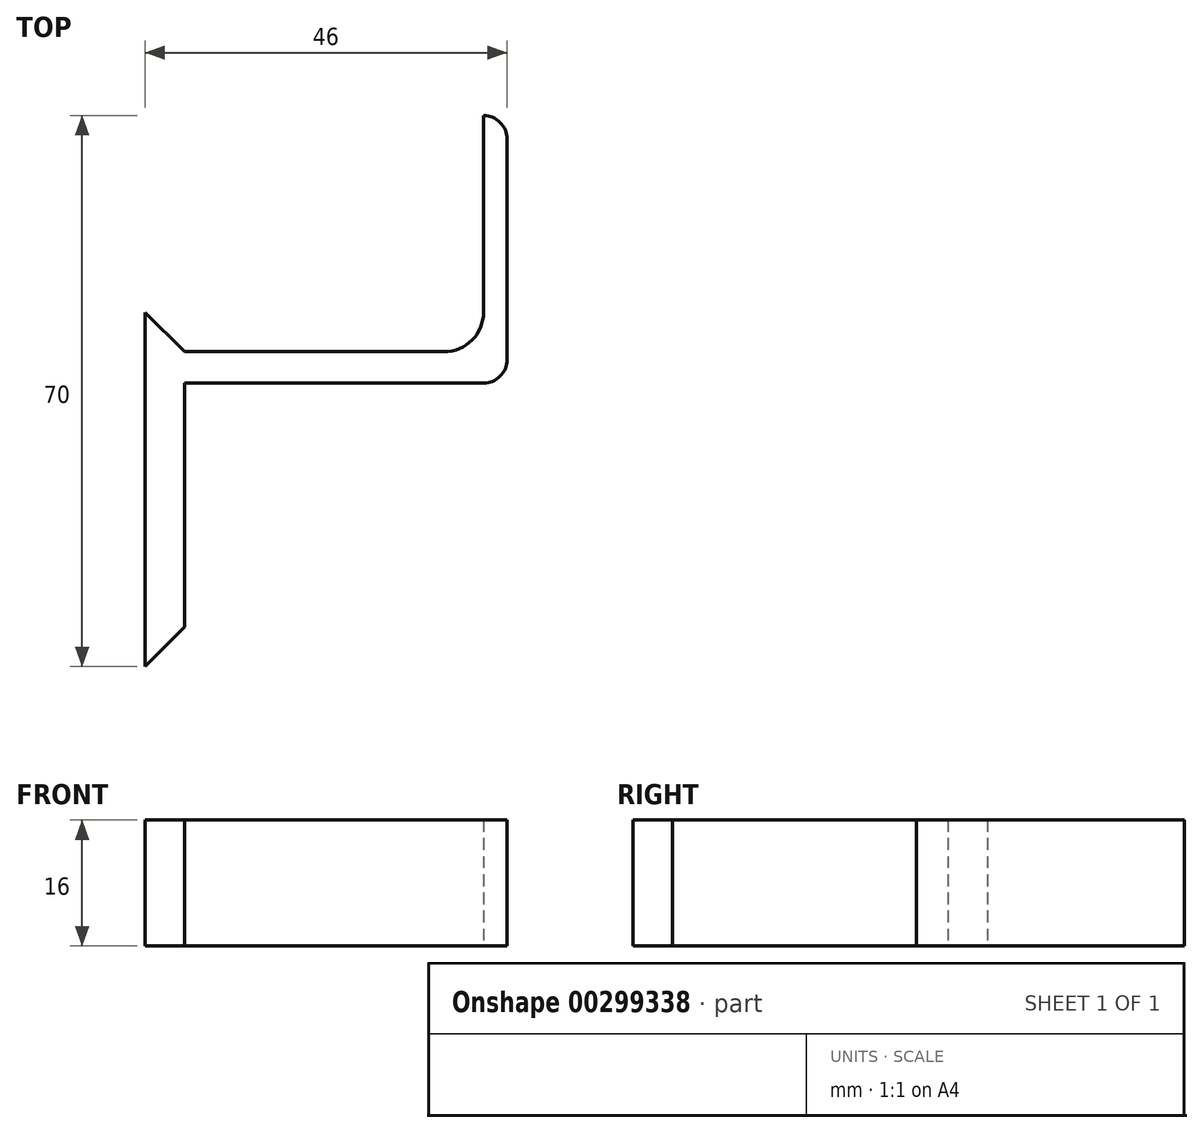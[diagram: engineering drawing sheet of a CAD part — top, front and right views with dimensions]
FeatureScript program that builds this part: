
annotation { "Feature Type Name" : "Feature", "Feature Type Description" : "" }
export const myFeature = defineFeature(function(context is Context, id is Id, definition is map)
    precondition{}
    {
        {
            var Q0;
            Q0=qCreatedBy(makeId("Top.planeOp"),FACE);
            var sketch = newSketch(context, id + "F0", { "sketchPlane" : qUnion([Q0])});
            skLineSegment(sketch, "E0", {"start": v(-35.28, 0) * mm, "end": v(-35.28, -40) * mm});
            skLineSegment(sketch, "E1", {"start": v(-35.28, 0) * mm, "end": v(2.72, 0) * mm});
            skLineSegment(sketch, "E2", {"start": v(2.72, 0) * mm, "end": v(2.72, 30) * mm});
            skLineSegment(sketch, "E3", {"start": v(2.72, 30) * mm, "end": v(5.72, 30) * mm});
            skLineSegment(sketch, "E4", {"start": v(5.72, 30) * mm, "end": v(5.72, 0) * mm});
            skLineSegment(sketch, "E5", {"start": v(5.72, 0) * mm, "end": v(2.72, 0) * mm});
            skLineSegment(sketch, "E6", {"start": v(5.72, 0) * mm, "end": v(5.72, -4) * mm});
            skLineSegment(sketch, "E7", {"start": v(5.72, -4) * mm, "end": v(-35.28, -4) * mm});
            skLineSegment(sketch, "E8", {"start": v(-35.28, 0) * mm, "end": v(-40.28, 0) * mm});
            skLineSegment(sketch, "E9", {"start": v(-40.28, 0) * mm, "end": v(-40.28, -40) * mm});
            skLineSegment(sketch, "E10", {"start": v(-40.28, -40) * mm, "end": v(-35.28, -40) * mm});
            skLineSegment(sketch, "E11", {"start": v(-40.28, 0) * mm, "end": v(-40.28, 5) * mm});
            skLineSegment(sketch, "E12", {"start": v(-40.28, 5) * mm, "end": v(-35.28, 5) * mm});
            skLineSegment(sketch, "E13", {"start": v(-35.28, 5) * mm, "end": v(-35.28, 0) * mm});
            skSolve(sketch);
        }
        {
            var Q0;
            Q0=makeQuery(id+"F0.imprint","IMPRINT",FACE,{"disambiguationData":[TD([[makeQuery(id+"F0.imprint","IMPRINT",EDGE,{"derivedFrom":sQuery(id+"F0.wireOp",EDGE,"E8")}),-1.0]])]});
            var Q1;
            {var subQ0=sQuery(id+"F0.wireOp",EDGE,"E8");Q1=makeQuery(id+"F0.imprint","IMPRINT",FACE,{"disambiguationData":[TD([[makeQuery(id+"F0.imprint","IMPRINT",EDGE,{"derivedFrom":subQ0}),1.0]])]});}
            var Q2;
            {var subQ0=sQuery(id+"F0.wireOp",EDGE,"E1");Q2=makeQuery(id+"F0.imprint","IMPRINT",FACE,{"disambiguationData":[TD([[makeQuery(id+"F0.imprint","IMPRINT",EDGE,{"derivedFrom":subQ0}),-1.0]])]});}
            var Q3;
            Q3=makeQuery(id+"F0.imprint","IMPRINT",FACE,{"disambiguationData":[TD([[makeQuery(id+"F0.imprint","IMPRINT",EDGE,{"derivedFrom":sQuery(id+"F0.wireOp",EDGE,"E2")}),-1.0]])]});
            extrude(context, id + "F1", {"entities" : qUnion([Q0, Q1, Q2, Q3]), "depth" : 16 * mm});
        }
        {
            var Q0;
            Q0=makeQuery(id+"F1.opExtrude","SWEPT_EDGE",EDGE,{"disambiguationData":[OSD([sQuery(id+"F0.wireOp",EDGE,"E12"),sQuery(id+"F0.wireOp",EDGE,"E13")])]});
            chamfer(context, id + "F2", {"entities" : qUnion([Q0]), "width" : 5 * mm, "tangentPropagation" : true});
        }
        {
            var Q0;
            Q0=makeQuery(id+"F1.opExtrude","SWEPT_EDGE",EDGE,{"disambiguationData":[OSD([sQuery(id+"F0.wireOp",EDGE,"E0"),sQuery(id+"F0.wireOp",EDGE,"E10")])]});
            chamfer(context, id + "F3", {"entities" : qUnion([Q0]), "width" : 5 * mm, "tangentPropagation" : true});
        }
        {
            var Q0;
            Q0=makeQuery(id+"F1.opExtrude","SWEPT_EDGE",EDGE,{"disambiguationData":[OSD([sQuery(id+"F0.wireOp",EDGE,"E1"),sQuery(id+"F0.wireOp",EDGE,"E2"),sQuery(id+"F0.wireOp",EDGE,"E5")])]});
            fillet(context, id + "F4", {"entities" : qUnion([Q0]), "radius" : 5 * mm, "tangentPropagation" : true, "allowEdgeOverflow" : false});
        }
        {
            var Q0;
            Q0=makeQuery(id+"F1.opExtrude","SWEPT_EDGE",EDGE,{"disambiguationData":[OSD([sQuery(id+"F0.wireOp",EDGE,"E6"),sQuery(id+"F0.wireOp",EDGE,"E7")])]});
            var Q1;
            Q1=makeQuery(id+"F1.opExtrude","SWEPT_EDGE",EDGE,{"disambiguationData":[OSD([sQuery(id+"F0.wireOp",EDGE,"E3"),sQuery(id+"F0.wireOp",EDGE,"E4")])]});
            fillet(context, id + "F5", {"entities" : qUnion([Q0, Q1]), "radius" : 3 * mm, "tangentPropagation" : true, "allowEdgeOverflow" : false});
        }
    });
